# Revit family: Camera-Security-Panasonic-FixedBox-Outdoor-Amba-4K_Vandal_Resistant_Weatherproof_Network-SPV781L2
name_source: partatom
category: Security Devices
revit_build: Autodesk Revit 2013 (Build: 20130531_2115(x64)
units: mm (PartAtom-declared; Revit-internal decimal feet)

## types (1)
- WV-SPV781L
    Alarm Input Or Output Specification = ALARM IN1 (DAY/NIGHT IN), ALARM IN2 (ALARM OUT), ALARM IN3 (AUX OUT, DAY/NIGHT OUT)
    Angle Of View = 97
    Audio In = Yes
    Audio Out = Yes
    Communication Ports = 10Base-T / 100Base-TX, RJ-45
    Cost = 0 $
    Date Last Modified = September, 15, 2016
    Day Or Night = Yes
    Default Elevation = 48 "
    Description = Security Camera, 4K, Vandal Resistant, Weatherproof, Network, SPV781L
    Equipment Abbreviation = SC
    Family Version = 1.0.0
    HFOV Max 169 = 97.00°
    HFOV Max 43 = 101.00°
    HFOV Min 169 = 17.00°
    HFOV Min 43 = 18.00°
    Has POE = Yes
    IP Or Analog = IP
    Indoor Or Outdoor = Outdoor
    Manufacturer = Panasonic
    Minimum Illumination = 0 lx
    Model = WV-SPV781L
    Model Disclaimer = Contact Panasonic for more information
    Mounting Positions = Mount Dependent or Surface Mount
    Operational Humidity = 10% to 90% (no condensation)
    Operational Temperature = -49°F - 122°F
    Pan Max = 180.00°
    Pan Min = -180.00°
    Panning Range = -180 to +180
    Part Description = Security Camera, 4K, Vandal Resistant, Weatherproof, Network, SPV781L
    Part Number = WV-SPV781L
    Power Active = 12.6 W
    Product Documentation Link = http://ssbu-t.psn-web.net
    Product Material = Paint - Panasonic - Silver
    Product Page URL = http://security.panasonic.com
    Provide Feedback = https://www.surveymonkey.com
    Regulatory Compliance = UL60950-1, UL60950-22, C-UL CAN/CSA C22.2 No.60950-1, CE, IEC60950-1 FCC Part15 ClassA, ICES003 ClassA, EN55023 ClassB, EN55022 ClassB, EN55024
    Storage Temperature = -49°F - 149°F
    Tilt Max = 115.00°
    Tilt Min = -115.00°
    Tilting Range = -115 to +115
    URL = http://security.panasonic.com
    VFOV Max 169 = 55.00°
    VFOV Max 43 = 76.00°
    VFOV Min 169 = 9.40°
    VFOV Min 43 = 13.00°
    Vandal Resistant = Yes
    Voltage DC = 12 V
    Weight = 5.73 lb
    Wide Dynamic Range = Yes
    Yaw Max = 200.00°
    Yaw Min = -115.00°
    Yawing Range = -115 to +200
    z Const Pan Handle Length = 19.488 "
    z Const Tilt Base Length = 9.843 "
    z Const Tilt Base2 Length = 19.685 "
    z Const Tilt Handle Length = 11.811 "
    z Const Yaw Axis Length = 7.874 "
    z Const Yaw Base Length = 10.236 "
    z Const Yaw Base2 Length = 17.323 "
    z Const Yaw Handle Length = 9.252 "
    z Const Zero = 0 "
    z VV Viewpoint Depth Max = 8.425 "
    z VV Viewpoint Depth Min = 8.146 "

## geometry (parser evidence)
native form markers: Sweep x4
no freeform markers — native parametric forms only
